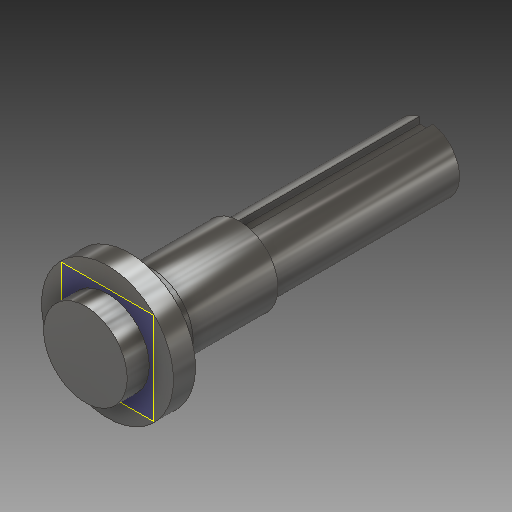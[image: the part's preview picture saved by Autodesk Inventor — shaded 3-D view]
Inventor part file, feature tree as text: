
AUTODESK INVENTOR PART (.ipt)
format: ipt  version: 2019 (Build 230136000, 136)  size: 157,184 bytes
history: native  units: in
note: dims shown in document units (in); Inventor stores cm internally (conversion verified against a paired STEP export)
features: sketch x5, other x3, plane x1
ambient origin geometry x8: Origin, YZ Plane, XZ Plane, XY Plane, X Axis, Y Axis, Z Axis, Center Point
bodies: Solid1 (feature_tree)
feature tree (9):
  other  "project handle part(1)_CPY.ipt"
  other  "Solid1::project handle part(1)_CPY.ipt"
  other  "TaggingFeature1"
  sketch  "Sketch1"  dims[d0=0.3937in]
  sketch  "Sketch2"
  sketch  "Sketch3"
  sketch  "Sketch4"
  sketch  "Sketch5"
  plane  "Work Plane1"
